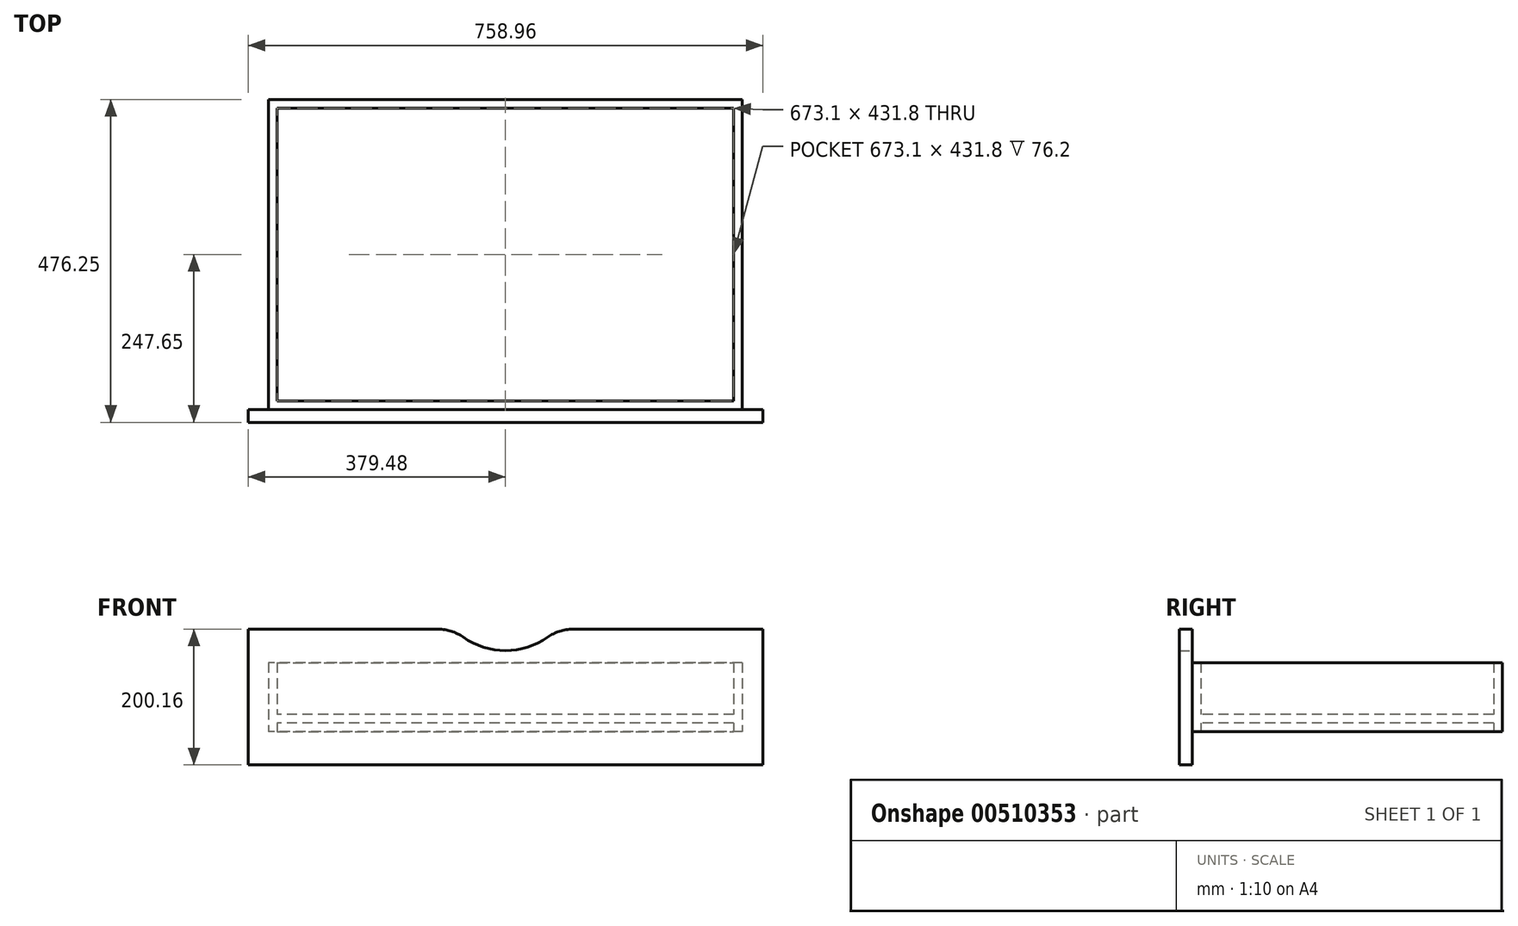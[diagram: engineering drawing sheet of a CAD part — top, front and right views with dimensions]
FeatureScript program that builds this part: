
annotation { "Feature Type Name" : "Feature", "Feature Type Description" : "" }
export const myFeature = defineFeature(function(context is Context, id is Id, definition is map)
    precondition{}
    {
        {
            var Q0;
            Q0=qCreatedBy(makeId("Top.planeOp"),FACE);
            var sketch = newSketch(context, id + "F0", { "sketchPlane" : qUnion([Q0])});
            skLineSegment(sketch, "E0.bottom", {"start": v(349.25, 228.6) * mm, "end": v(-349.25, 228.6) * mm});
            skLineSegment(sketch, "E0.top", {"start": v(349.25, -228.6) * mm, "end": v(-349.25, -228.6) * mm});
            skLineSegment(sketch, "E0.left", {"start": v(349.25, 228.6) * mm, "end": v(349.25, -228.6) * mm});
            skLineSegment(sketch, "E0.right", {"start": v(-349.25, 228.6) * mm, "end": v(-349.25, -228.6) * mm});
            skPoint(sketch, "E0.middle", {"position": v(0, 0) * mm});
            skLineSegment(sketch, "E1", {"start": v(-336.55, 215.9) * mm, "end": v(-349.25, 228.6) * mm});
            skLineSegment(sketch, "E2", {"start": v(-336.55, 215.9) * mm, "end": v(-336.55, -228.6) * mm});
            skLineSegment(sketch, "E3", {"start": v(336.55, 215.9) * mm, "end": v(349.25, 228.6) * mm});
            skLineSegment(sketch, "E4", {"start": v(336.55, 215.9) * mm, "end": v(336.55, -228.6) * mm});
            skLineSegment(sketch, "E5", {"start": v(-336.55, 215.9) * mm, "end": v(336.55, 215.9) * mm});
            skLineSegment(sketch, "E6", {"start": v(-336.55, -228.6) * mm, "end": v(-336.55, -215.9) * mm});
            skLineSegment(sketch, "E7", {"start": v(-336.55, -215.9) * mm, "end": v(336.55, -215.9) * mm});
            skSolve(sketch);
        }
        {
            var Q0;
            Q0 = qSketchRegion(id + "F0", true);
            extrude(context, id + "F1", {"entities" : qUnion([Q0]), "depth" : 101.6 * mm});
        }
        {
            var Q0;
            Q0=makeQuery(id+"F1.opExtrude","SWEPT_FACE",FACE,{"disambiguationData":[OSD([sQuery(id+"F0.wireOp",EDGE,"E5")])]});
            var sketch = newSketch(context, id + "F2", { "sketchPlane" : qUnion([Q0])});
            skLineSegment(sketch, "E8", {"start": v(-336.55, 0) * mm, "end": v(-336.55, 6.35) * mm});
            skLineSegment(sketch, "E9", {"start": v(-336.55, 6.35) * mm, "end": v(336.55, 6.35) * mm});
            skLineSegment(sketch, "E10", {"start": v(336.55, 6.35) * mm, "end": v(336.55, 12.7) * mm});
            skLineSegment(sketch, "E11", {"start": v(336.55, 12.7) * mm, "end": v(-336.55, 12.7) * mm});
            skLineSegment(sketch, "E12", {"start": v(-336.55, 12.7) * mm, "end": v(-336.55, 6.35) * mm});
            skSolve(sketch);
        }
        {
            var Q0;
            Q0=sQuery(id+"F2.wireOp",EDGE,"E11");
            extrude(context, id + "F3", {"bodyType" : ToolBodyType.SURFACE, "surfaceEntities" : qUnion([Q0]), "depth" : 431.8 * mm});
        }
        {
            var Q0;
            Q0=makeQuery(id+"F3.opExtrude","SWEPT_FACE",FACE,{"disambiguationData":[OSD([sQuery(id+"F2.wireOp",EDGE,"E11")])]});
            extrude(context, id + "F4", {"entities" : qUnion([Q0]), "operationType" : NewBodyOperationType.ADD, "depth" : 12.7 * mm});
        }
        {
            var Q0;
            Q0=makeQuery(id+"F1.opExtrude","SWEPT_FACE",FACE,{"disambiguationData":[OSD([sQuery(id+"F0.wireOp",EDGE,"E0.top")])]});
            var sketch = newSketch(context, id + "F5", { "sketchPlane" : qUnion([Q0])});
            skPoint(sketch, "E13.endSnap0", {"position": v(0, 101.6) * mm});
            skLineSegment(sketch, "E14.top", {"start": v(379.48, -49.28) * mm, "end": v(-379.48, -49.28) * mm});
            skLineSegment(sketch, "E14.left", {"start": v(379.48, 150.88) * mm, "end": v(379.48, -49.28) * mm});
            skLineSegment(sketch, "E14.right", {"start": v(-379.48, 150.88) * mm, "end": v(-379.48, -49.28) * mm});
            skPoint(sketch, "E14.middle", {"position": v(0, 50.8) * mm});
            skArc(sketch, "E15", {"start": v(-62.34, 139.2) * mm, "mid": v(0, 119.35) * mm, "end": v(62.34, 139.2) * mm});
            skLineSegment(sketch, "E16", {"start": v(99.05, 150.88) * mm, "end": v(379.48, 150.88) * mm});
            skLineSegment(sketch, "E17", {"start": v(-99.05, 150.88) * mm, "end": v(-379.48, 150.88) * mm});
            skPoint(sketch, "E18.visualSharp", {"position": v(76.2, 150.88) * mm});
            skArc(sketch, "E18.filletArc", {"start": v(99.05, 150.88) * mm, "mid": v(79.79, 147.88) * mm, "end": v(62.34, 139.2) * mm});
            skPoint(sketch, "E19.visualSharp", {"position": v(-76.2, 150.88) * mm});
            skArc(sketch, "E19.filletArc", {"start": v(-62.34, 139.2) * mm, "mid": v(-79.79, 147.88) * mm, "end": v(-99.05, 150.88) * mm});
            skSolve(sketch);
        }
        {
            var Q0;
            {var subQ0=sQuery(id+"F0.wireOp",EDGE,"E0.top");Q0=makeQuery(id+"F5.imprint","IMPRINT",FACE,{"disambiguationData":[TD([[makeQuery(id+"F5.imprint","IMPRINT",EDGE,{"derivedFrom":makeQuery(id+"F1.opExtrude","CAP_EDGE",EDGE,{"disambiguationData":[OSD([subQ0])],"isStart":true})}),-1.0]])]});}
            var Q1;
            Q1=makeQuery(id+"F5.imprint","IMPRINT",FACE,{"disambiguationData":[TD([[makeQuery(id+"F5.imprint","IMPRINT",EDGE,{"derivedFrom":sQuery(id+"F5.wireOp",EDGE,"E14.top")}),-1.0]])]});
            extrude(context, id + "F6", {"entities" : qUnion([Q0, Q1]), "operationType" : NewBodyOperationType.ADD, "depth" : 19.05 * mm});
        }
    });
